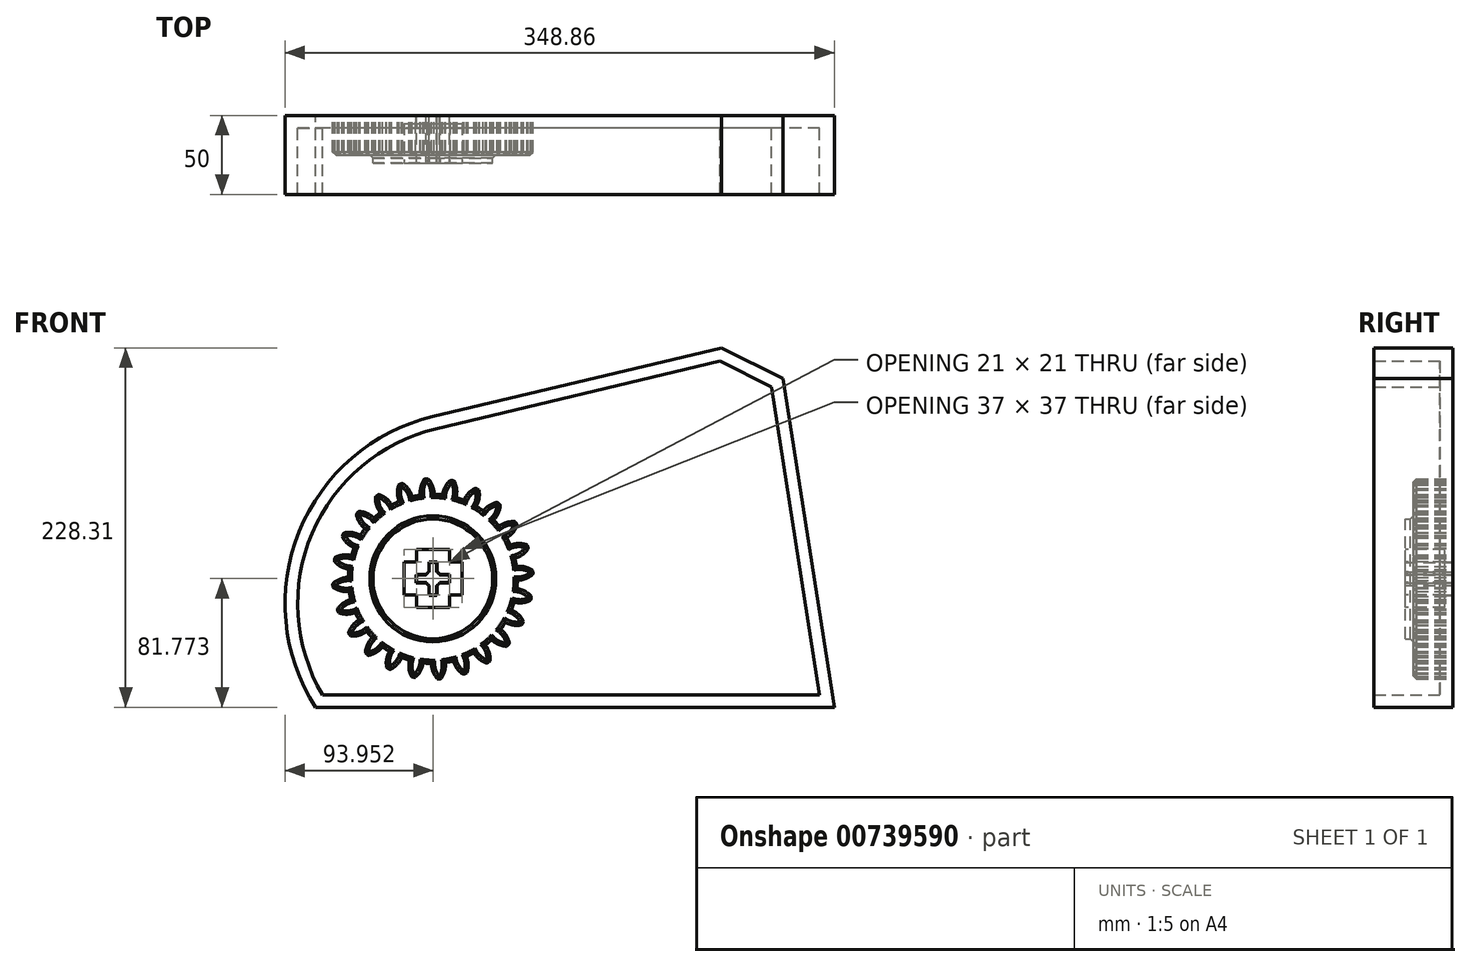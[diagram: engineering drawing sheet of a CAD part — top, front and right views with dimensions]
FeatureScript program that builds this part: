
annotation { "Feature Type Name" : "Feature", "Feature Type Description" : "" }
export const myFeature = defineFeature(function(context is Context, id is Id, definition is map)
    precondition{}
    {
        {
            var Q0;
            Q0=qCreatedBy(makeId("Front.planeOp"),FACE);
            var sketch = newSketch(context, id + "F0", { "sketchPlane" : qUnion([Q0])});
            skCircle(sketch, "E0", {"center": v(0, 0) * mm, "radius": 53.72 * mm});
            skCircle(sketch, "E1", {"center": v(0, 0) * mm, "radius": 58.67 * mm, "construction": true});
            skCircle(sketch, "E2", {"center": v(0, 0) * mm, "radius": 63.5 * mm, "construction": true});
            skLineSegment(sketch, "E3", {"start": v(0, 0) * mm, "end": v(0, 101.5) * mm, "construction": true});
            skLineSegment(sketch, "E4", {"start": v(0, 0) * mm, "end": v(-7.23, 110.28) * mm, "construction": true});
            skLineSegment(sketch, "E5", {"start": v(0, 58.67) * mm, "end": v(-75.03, 58.67) * mm, "construction": true});
            skLineSegment(sketch, "E6", {"start": v(0, 58.67) * mm, "end": v(-75.24, 31.29) * mm, "construction": true});
            skCircle(sketch, "E7", {"center": v(0, 0) * mm, "radius": 55.14 * mm, "construction": true});
            skCircle(sketch, "E8", {"center": v(0, 58.67) * mm, "radius": 14.6 * mm, "construction": true});
            skCircle(sketch, "E9", {"center": v(-13.72, 53.68) * mm, "radius": 14.6 * mm, "construction": true});
            skArc(sketch, "E10", {"start": v(0, 58.67) * mm, "mid": v(-1.2, 61.2) * mm, "end": v(-2.86, 63.44) * mm});
            skArc(sketch, "E11", {"start": v(0.88, 53.71) * mm, "mid": v(0.66, 56.23) * mm, "end": v(0, 58.67) * mm});
            skArc(sketch, "E12.MirrorCS", {"start": v(-7.66, 58.17) * mm, "mid": v(-6.8, 60.82) * mm, "end": v(-5.45, 63.27) * mm});
            skArc(sketch, "E13.MirrorCS", {"start": v(-7.88, 53.14) * mm, "mid": v(-8, 55.67) * mm, "end": v(-7.66, 58.17) * mm});
            skArc(sketch, "E14", {"start": v(-2.86, 63.44) * mm, "mid": v(-4.16, 63.54) * mm, "end": v(-5.45, 63.27) * mm});
            skCircle(sketch, "E15", {"center": v(0, 0) * mm, "radius": 38 * mm});
            skLineSegment(sketch, "E16.bottom", {"start": v(-2.5, -10.5) * mm, "end": v(2.5, -10.5) * mm});
            skLineSegment(sketch, "E16.top", {"start": v(-2.5, 10.5) * mm, "end": v(2.5, 10.5) * mm});
            skLineSegment(sketch, "E16.left", {"start": v(-2.5, -10.5) * mm, "end": v(-2.5, 10.5) * mm});
            skLineSegment(sketch, "E16.right", {"start": v(2.5, -10.5) * mm, "end": v(2.5, 10.5) * mm});
            skLineSegment(sketch, "E17.bottom", {"start": v(-10.5, -2.5) * mm, "end": v(10.5, -2.5) * mm});
            skLineSegment(sketch, "E17.top", {"start": v(-10.5, 2.5) * mm, "end": v(10.5, 2.5) * mm});
            skLineSegment(sketch, "E17.left", {"start": v(-10.5, -2.5) * mm, "end": v(-10.5, 2.5) * mm});
            skLineSegment(sketch, "E17.right", {"start": v(10.5, -2.5) * mm, "end": v(10.5, 2.5) * mm});
            skCircle(sketch, "E18", {"center": v(0, 0) * mm, "radius": 5 * mm});
            skSolve(sketch);
        }
        {
            var Q0;
            {var subQ0=sQuery(id+"F0.wireOp",EDGE,"E0");var subQ1=makeQuery(id+"F0.imprint","INTERSECT",VERTEX,{"derivedFrom":[subQ0,sQuery(id+"F0.wireOp",EDGE,"E11")]});Q0=makeQuery(id+"F0.imprint","IMPRINT",FACE,{"disambiguationData":[TD([[makeQuery(id+"F0.imprint","IMPRINT",EDGE,{"disambiguationData":[TD([[subQ1,-1.0]])],"derivedFrom":subQ0}),1.0]])]});}
            var Q1;
            Q1=makeQuery(id+"F0.imprint","IMPRINT",FACE,{"disambiguationData":[TD([[makeQuery(id+"F0.imprint","IMPRINT",EDGE,{"derivedFrom":sQuery(id+"F0.wireOp",EDGE,"E10")}),1.0]])]});
            extrude(context, id + "F1", {"entities" : qUnion([Q0, Q1]), "depth" : 25 * mm, "offsetDistance" : 25 * mm});
        }
        {
            var Q0;
            Q0=makeQuery(id+"F1.opExtrude","SWEPT_BODY",BODY,{"disambiguationData":[OSD([sQuery(id+"F0.wireOp",EDGE,"E0"),sQuery(id+"F0.wireOp",EDGE,"E10"),sQuery(id+"F0.wireOp",EDGE,"E11"),sQuery(id+"F0.wireOp",EDGE,"E12.MirrorCS"),sQuery(id+"F0.wireOp",EDGE,"E13.MirrorCS"),sQuery(id+"F0.wireOp",EDGE,"E14")])]});
            var Q1;
            Q1=makeQuery(id+"F1.opExtrude","SWEPT_FACE",FACE,{"disambiguationData":[OSD([sQuery(id+"F0.wireOp",EDGE,"E0")])]});
            circularPattern(context, id + "F2", {"entities" : qUnion([Q0]), "axis" : qUnion([Q1]), "angle" : 360 * degree, "instanceCount" : 24, "equalSpace" : true});
        }
        {
            var Q0;
            Q0=makeQuery(id+"F0.imprint","IMPRINT",FACE,{"disambiguationData":[TD([[makeQuery(id+"F0.imprint","IMPRINT",EDGE,{"derivedFrom":sQuery(id+"F0.wireOp",EDGE,"E15")}),1.0]])]});
            extrude(context, id + "F3", {"entities" : qUnion([Q0]), "operationType" : NewBodyOperationType.ADD, "depth" : 30 * mm, "offsetDistance" : 25 * mm});
        }
        {
            var Q0;
            {var subQ0=makeQuery(id+"F1.opExtrude","CAP_FACE",FACE,{"disambiguationData":[OSD([sQuery(id+"F0.wireOp",EDGE,"E0"),sQuery(id+"F0.wireOp",EDGE,"E10"),sQuery(id+"F0.wireOp",EDGE,"E11"),sQuery(id+"F0.wireOp",EDGE,"E12.MirrorCS"),sQuery(id+"F0.wireOp",EDGE,"E13.MirrorCS"),sQuery(id+"F0.wireOp",EDGE,"E14"),sQuery(id+"F0.wireOp",EDGE,"E15")])],"isStart":false});Q0=makeQuery(id+"F3.boolean.opBoolean","MERGE",FACE,{"derivedFrom":[subQ0,makeQuery(id+"F2.opPattern","COPY",FACE,{"derivedFrom":subQ0,"instanceName":"1"}),makeQuery(id+"F2.opPattern","COPY",FACE,{"derivedFrom":subQ0,"instanceName":"2"}),makeQuery(id+"F2.opPattern","COPY",FACE,{"derivedFrom":subQ0,"instanceName":"3"}),makeQuery(id+"F2.opPattern","COPY",FACE,{"derivedFrom":subQ0,"instanceName":"4"}),makeQuery(id+"F2.opPattern","COPY",FACE,{"derivedFrom":subQ0,"instanceName":"5"}),makeQuery(id+"F2.opPattern","COPY",FACE,{"derivedFrom":subQ0,"instanceName":"6"}),makeQuery(id+"F2.opPattern","COPY",FACE,{"derivedFrom":subQ0,"instanceName":"7"}),makeQuery(id+"F2.opPattern","COPY",FACE,{"derivedFrom":subQ0,"instanceName":"8"}),makeQuery(id+"F2.opPattern","COPY",FACE,{"derivedFrom":subQ0,"instanceName":"9"}),makeQuery(id+"F2.opPattern","COPY",FACE,{"derivedFrom":subQ0,"instanceName":"10"}),makeQuery(id+"F2.opPattern","COPY",FACE,{"derivedFrom":subQ0,"instanceName":"11"}),makeQuery(id+"F2.opPattern","COPY",FACE,{"derivedFrom":subQ0,"instanceName":"12"}),makeQuery(id+"F2.opPattern","COPY",FACE,{"derivedFrom":subQ0,"instanceName":"13"}),makeQuery(id+"F2.opPattern","COPY",FACE,{"derivedFrom":subQ0,"instanceName":"14"}),makeQuery(id+"F2.opPattern","COPY",FACE,{"derivedFrom":subQ0,"instanceName":"15"}),makeQuery(id+"F2.opPattern","COPY",FACE,{"derivedFrom":subQ0,"instanceName":"16"}),makeQuery(id+"F2.opPattern","COPY",FACE,{"derivedFrom":subQ0,"instanceName":"17"}),makeQuery(id+"F2.opPattern","COPY",FACE,{"derivedFrom":subQ0,"instanceName":"18"}),makeQuery(id+"F2.opPattern","COPY",FACE,{"derivedFrom":subQ0,"instanceName":"19"}),makeQuery(id+"F2.opPattern","COPY",FACE,{"derivedFrom":subQ0,"instanceName":"20"}),makeQuery(id+"F2.opPattern","COPY",FACE,{"derivedFrom":subQ0,"instanceName":"21"}),makeQuery(id+"F2.opPattern","COPY",FACE,{"derivedFrom":subQ0,"instanceName":"22"}),makeQuery(id+"F2.opPattern","COPY",FACE,{"derivedFrom":subQ0,"instanceName":"23"})]});}
            chamfer(context, id + "F4", {"entities" : qUnion([Q0]), "width" : 2 * mm, "tangentPropagation" : true});
        }
        {
            var Q0;
            Q0=qCreatedBy(makeId("Front.planeOp"),FACE);
            var sketch = newSketch(context, id + "F5", { "sketchPlane" : qUnion([Q0])});
            skLineSegment(sketch, "E19", {"start": v(255.04, -81.57) * mm, "end": v(222.29, 127.22) * mm});
            skLineSegment(sketch, "E20", {"start": v(222.29, 127.22) * mm, "end": v(183.25, 146.74) * mm});
            skLineSegment(sketch, "E21", {"start": v(183.25, 146.74) * mm, "end": v(0, 103.03) * mm});
            skLineSegment(sketch, "E22", {"start": v(255.04, -81.57) * mm, "end": v(-74.6, -81.57) * mm});
            skArc(sketch, "E23", {"start": v(0, 103.03) * mm, "mid": v(-84.92, 29.97) * mm, "end": v(-74.6, -81.57) * mm});
            skSolve(sketch);
        }
        {
            var Q0;
            Q0=makeQuery(id+"F5.imprint","IMPRINT",FACE,{"disambiguationData":[TD([[makeQuery(id+"F5.imprint","IMPRINT",EDGE,{"derivedFrom":sQuery(id+"F5.wireOp",EDGE,"E19")}),1.0]])]});
            var sketch = newSketch(context, id + "F6", { "sketchPlane" : qUnion([Q0])});
            skLineSegment(sketch, "E24.bottom", {"start": v(-2.37, -10.3) * mm, "end": v(2.63, -10.3) * mm});
            skLineSegment(sketch, "E24.top", {"start": v(-2.37, 10.7) * mm, "end": v(2.63, 10.7) * mm});
            skLineSegment(sketch, "E24.left", {"start": v(-2.37, -10.3) * mm, "end": v(-2.37, 10.7) * mm});
            skLineSegment(sketch, "E24.right", {"start": v(2.63, -10.3) * mm, "end": v(2.63, 10.7) * mm});
            skLineSegment(sketch, "E25.bottom", {"start": v(-10.37, -2.3) * mm, "end": v(10.63, -2.3) * mm});
            skLineSegment(sketch, "E25.top", {"start": v(-10.37, 2.7) * mm, "end": v(10.63, 2.7) * mm});
            skLineSegment(sketch, "E25.left", {"start": v(-10.37, -2.3) * mm, "end": v(-10.37, 2.7) * mm});
            skLineSegment(sketch, "E25.right", {"start": v(10.63, -2.3) * mm, "end": v(10.63, 2.7) * mm});
            skCircle(sketch, "E26", {"center": v(0.13, 0.2) * mm, "radius": 5 * mm});
            skSolve(sketch);
        }
        {
            var Q0;
            {var subQ7=sQuery(id+"F6.wireOp",EDGE,"E24.bottom");Q0=makeQuery(id+"F6.imprint","IMPRINT",FACE,{"disambiguationData":[TD([[makeQuery(id+"F6.imprint","IMPRINT",EDGE,{"derivedFrom":subQ7}),-1.0]])]});}
            extrude(context, id + "F7", {"entities" : qUnion([Q0]), "depth" : 50 * mm, "offsetDistance" : 25 * mm});
        }
        {
            var Q0;
            Q0=makeQuery(id+"F7.opExtrude","CAP_FACE",FACE,{"disambiguationData":[OSD([sQuery(id+"F5.wireOp",EDGE,"E19"),sQuery(id+"F5.wireOp",EDGE,"E20"),sQuery(id+"F5.wireOp",EDGE,"E21"),sQuery(id+"F5.wireOp",EDGE,"E22"),sQuery(id+"F5.wireOp",EDGE,"E23")])],"isStart":false});
            shell(context, id + "F8", {"entities" : qUnion([Q0]), "thickness" : 8 * mm});
        }
        {
            var Q0;
            {var subQ0=sQuery(id+"F6.wireOp",EDGE,"E26");var subQ1=sQuery(id+"F6.wireOp",EDGE,"E25.right");var subQ2=sQuery(id+"F6.wireOp",EDGE,"E25.left");var subQ3=sQuery(id+"F6.wireOp",EDGE,"E25.top");var subQ4=sQuery(id+"F6.wireOp",EDGE,"E25.bottom");var subQ5=sQuery(id+"F6.wireOp",EDGE,"E24.right");var subQ6=sQuery(id+"F6.wireOp",EDGE,"E24.left");var subQ7=sQuery(id+"F6.wireOp",EDGE,"E24.top");var subQ8=sQuery(id+"F6.wireOp",EDGE,"E24.bottom");var subQ9=sQuery(id+"F5.wireOp",EDGE,"E23");var subQ10=sQuery(id+"F5.wireOp",EDGE,"E22");var subQ11=sQuery(id+"F5.wireOp",EDGE,"E21");var subQ12=sQuery(id+"F5.wireOp",EDGE,"E20");var subQ13=sQuery(id+"F5.wireOp",EDGE,"E19");Q0=makeQuery(id+"F8.opShell","OFFSET_FACE",FACE,{"disambiguationData":[OSD([subQ13,subQ12,subQ11,subQ10,subQ9,subQ8,subQ7,subQ6,subQ5,subQ4,subQ3,subQ2,subQ1,subQ0]),TDD([makeQuery(id+"F7.opExtrude","CAP_FACE",FACE,{"disambiguationData":[OSD([subQ13,subQ12,subQ11,subQ10,subQ9,subQ8,subQ7,subQ6,subQ5,subQ4,subQ3,subQ2,subQ1,subQ0])],"isStart":false})])]});}
            extrude(context, id + "F9", {"entities" : qUnion([Q0]), "operationType" : NewBodyOperationType.REMOVE, "oppositeDirection" : true, "depth" : 45 * mm, "offsetDistance" : 25 * mm});
        }
    });
